# Revit family: BuroSeating_Buro Mentor Upholstery
name_source: partatom
category: Furniture
units: mm (PartAtom-declared; Revit-internal decimal feet)

## family parameters
Always vertical = Yes
Cut with Voids When Loaded = No
OmniClass Number = 23.40.70.14.64.11
OmniClass Title = Office Furniture
Room Calculation Point = No
Shared = Yes
Work Plane-Based = No

## types (8) — shared parameters
ArmRestMaterial = BuroSeating_Plastic_Black
ArmRestSupportMaterial = BuroSeating_Aluminium_Black
Assembly Code = E2020
BackFrameMaterial = BuroSeating_Plastic_Black
BackPanel = Yes
BackPanelMaterial = BuroSeating_Plastic_Black
BackRestMaterial = BuroSeating_Fabric_Black
BackSupportMaterial = BuroSeating_Aluminium_Black
BottomLiftMaterial = BuroSeating_Plastic_Black
CastorMaterial = BuroSeating_Aluminium_Black
CastorWheelMaterial = BuroSeating_Aluminium_Black
FrameMaterial = BuroSeating_Aluminium_Black
HeadRestMaterial = BuroSeating_Fabric_Black
HeadRestSupportMaterial = BuroSeating_Plastic_Black
Manufacturer = Buro Seating
Model = 132-23
NominalDepth = 635 mm
NominalHeight = 1210 mm
NominalSeatDepthRange = 430-480d
NominalSeatHeight = 475-595h
NominalWidth = 495 mm
ProductGroup = Mentor
ProductPageURL AU = https://buroseating.com
ProductPageURL NZ = https://buroseating.co.nz
ProductRange = Buro
SeatDepth = 455 mm
SeatLeverFrameMaterial = BuroSeating_Aluminium_Black
SeatLeverHandleMaterial = BuroSeating_Aluminium_Black
SeatMaterial = BuroSeating_Fabric_Black
SeatSupportMaterial = BuroSeating_Plastic_Black
SeatTiltMaterial = BuroSeating_Aluminium_Black
SeatWidth = 520 mm
TopLiftMaterial = BuroSeating_Metal_Chrome_Semi-Polished
Type Comments = Seat Height 475-595mm High
URL = https://buroseating.co.nz
URL AU = https://buroseating.com
WarrantyDescription = Full 5 year guarantee (excluding upholstery)
zero-valued in all types: Default Elevation

## per-type parameters (varying)
| type | BaseMaterial | Description | SeatArms | SeatHeadRest |
| Buro Mentor Upholstery 132-23 Aluminium Base | BuroSeating_Metal_Chrome_Semi-Polished | Buro Mentor Upholstered Aluminium Base with Arms | No | No |
| Buro Mentor Upholstery 132-23 Aluminium Base with Arms | BuroSeating_Metal_Chrome_Semi-Polished | Buro Mentor Upholstered Aluminium Base with Arms | Yes | No |
| Buro Mentor Upholstery 132-23 Aluminium Base with Arms and Headrest | BuroSeating_Metal_Chrome_Semi-Polished | Buro Mentor Upholstered Aluminium Base with Arms and Headrest | Yes | Yes |
| Buro Mentor Upholstery 132-23 Aluminium Base with Headrest | BuroSeating_Metal_Chrome_Semi-Polished | Buro Mentor Upholstered Aluminium Base Nylon with Head Rest | No | Yes |
| Buro Mentor Upholstery 132-23 Nylon Base | BuroSeating_Plastic_Black | Buro Mentor Upholstered Nylon Base with Arms | No | No |
| Buro Mentor Upholstery 132-23 Nylon Base with Arms | BuroSeating_Plastic_Black | Buro Mentor Upholstered Nylon Base with Arms | Yes | No |
| Buro Mentor Upholstery 132-23 Nylon Base with Arms and Headrest | BuroSeating_Plastic_Black | Buro Mentor Upholstered Nylon Base with Arms and Headrest | Yes | Yes |
| Buro Mentor Upholstery 132-23 Nylon Base with Headrest | BuroSeating_Plastic_Black | Buro Mentor Upholstered Nylon Base with Head Rest | No | Yes |

## geometry (parser evidence)
native form markers: Sweep x6
no freeform markers — native parametric forms only
